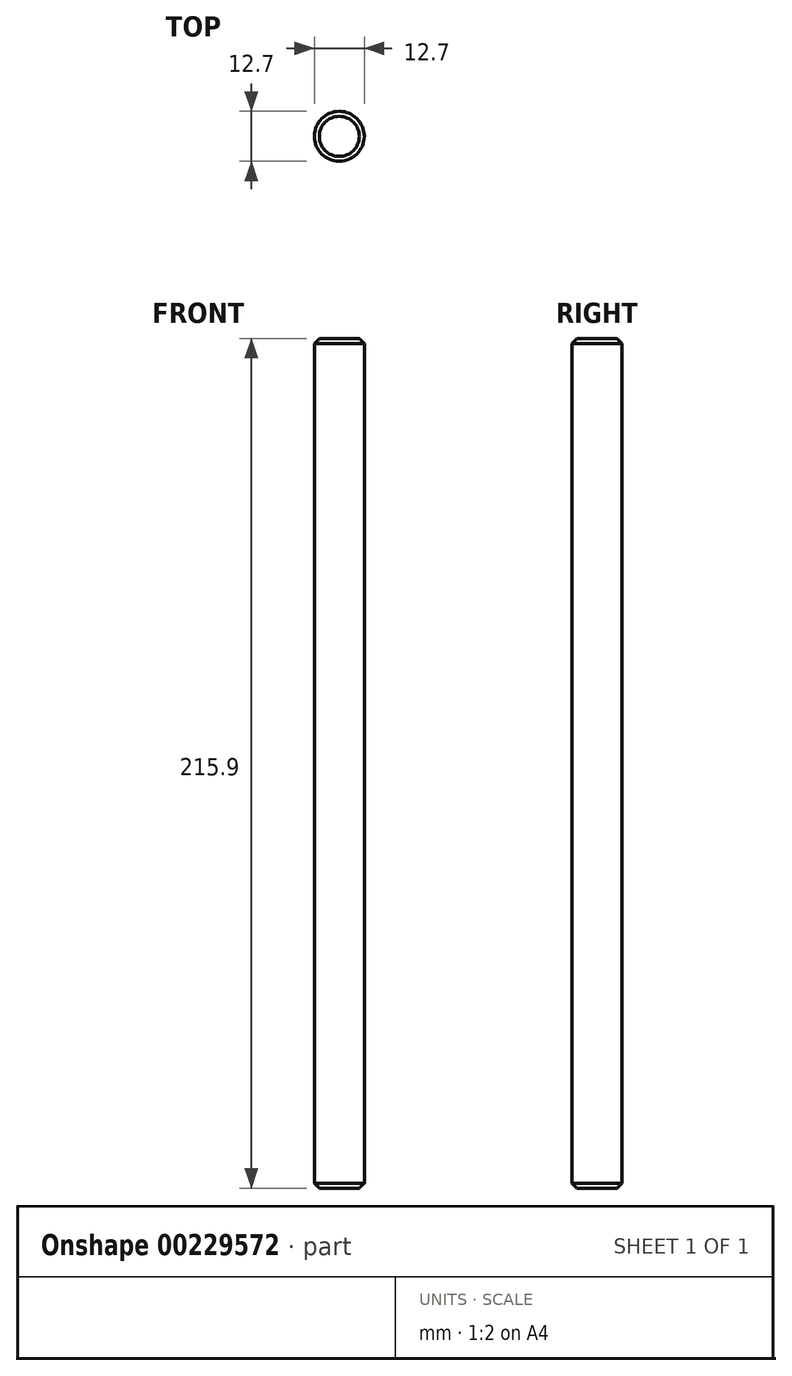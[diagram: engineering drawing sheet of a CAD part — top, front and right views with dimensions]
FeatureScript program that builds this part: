
annotation { "Feature Type Name" : "Feature", "Feature Type Description" : "" }
export const myFeature = defineFeature(function(context is Context, id is Id, definition is map)
    precondition{}
    {
        {
            var Q0;
            Q0=qCreatedBy(makeId("Top.planeOp"),FACE);
            var sketch = newSketch(context, id + "F0", { "sketchPlane" : qUnion([Q0])});
            skCircle(sketch, "E0", {"center": v(0, 0) * mm, "radius": 6.35 * mm});
            skSolve(sketch);
        }
        {
            var Q0;
            Q0 = qSketchRegion(id + "F0", true);
            extrude(context, id + "F1", {"entities" : qUnion([Q0]), "depth" : 215.9 * mm});
        }
        {
            var Q0;
            Q0=makeQuery(id+"F1.opExtrude","SWEPT_FACE",FACE,{"disambiguationData":[OSD([sQuery(id+"F0.wireOp",EDGE,"E0")])]});
            chamfer(context, id + "F2", {"entities" : qUnion([Q0]), "width" : 1.27 * mm, "tangentPropagation" : true});
        }
    });
